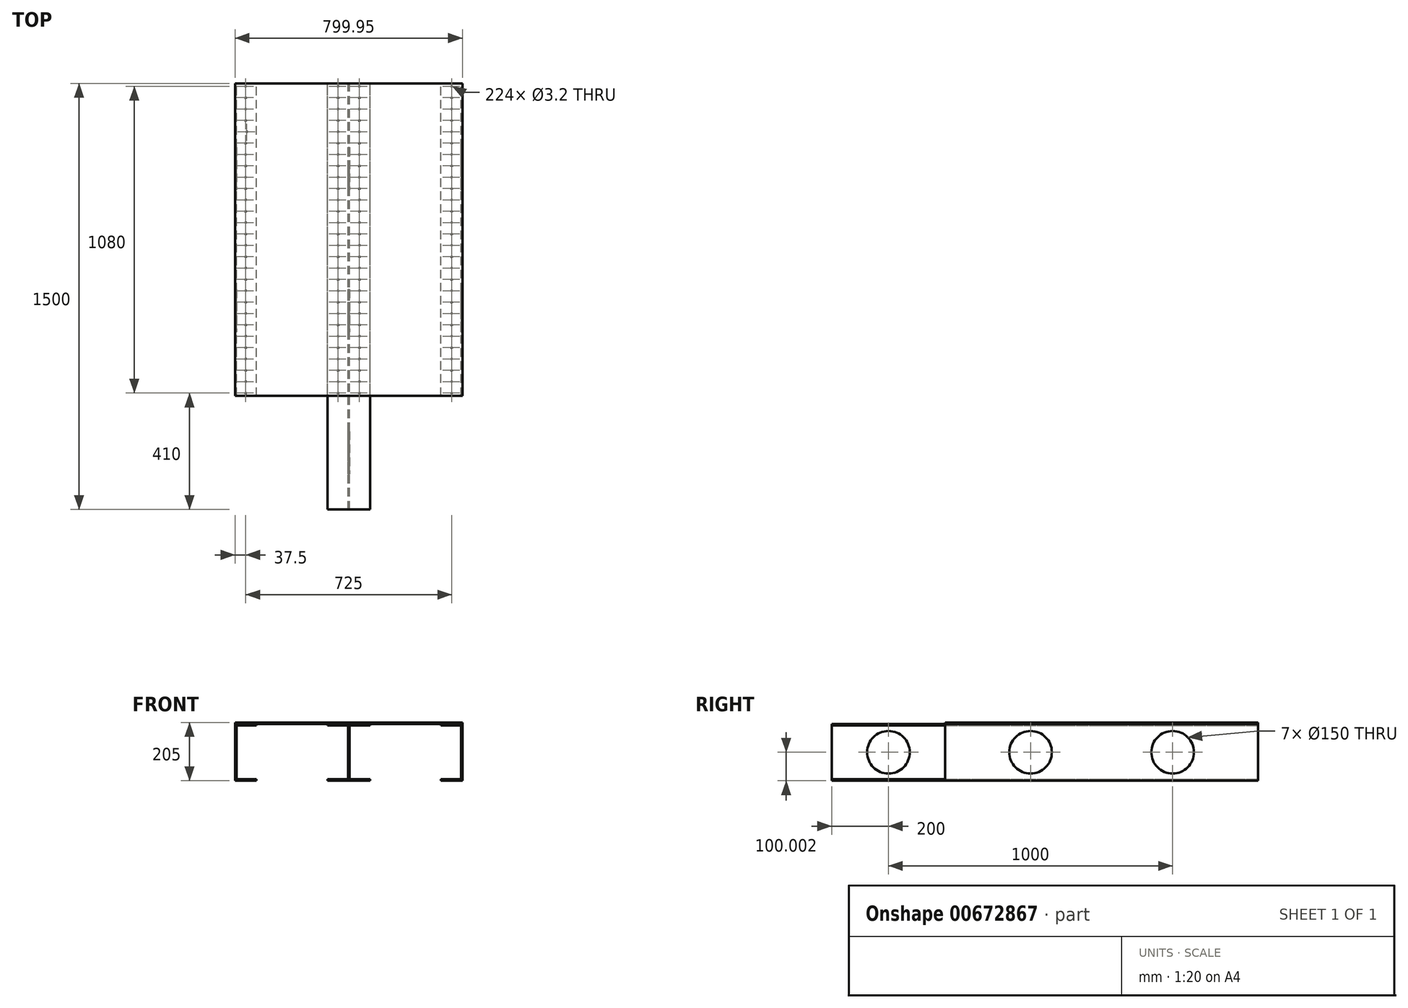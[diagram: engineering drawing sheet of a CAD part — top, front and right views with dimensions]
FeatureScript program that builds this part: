
annotation { "Feature Type Name" : "Feature", "Feature Type Description" : "" }
export const myFeature = defineFeature(function(context is Context, id is Id, definition is map)
    precondition{}
    {
        {
            var Q0;
            Q0=qCreatedBy(makeId("Front.planeOp"),FACE);
            var sketch = newSketch(context, id + "F0", { "sketchPlane" : qUnion([Q0])});
            skLineSegment(sketch, "E0", {"start": v(180.44, 90.06) * mm, "end": v(255.44, 90.06) * mm});
            skLineSegment(sketch, "E1", {"start": v(255.44, -109.94) * mm, "end": v(180.44, -109.94) * mm});
            skLineSegment(sketch, "E2", {"start": v(180.44, -109.94) * mm, "end": v(180.44, -104.94) * mm});
            skLineSegment(sketch, "E3", {"start": v(180.44, -104.94) * mm, "end": v(250.44, -104.94) * mm});
            skLineSegment(sketch, "E4", {"start": v(250.44, -104.94) * mm, "end": v(250.44, 85.06) * mm});
            skLineSegment(sketch, "E5", {"start": v(250.44, 85.06) * mm, "end": v(180.44, 85.06) * mm});
            skLineSegment(sketch, "E6", {"start": v(180.44, 85.06) * mm, "end": v(180.44, 90.06) * mm});
            skLineSegment(sketch, "E7", {"start": v(255.44, 90.06) * mm, "end": v(255.44, -109.94) * mm});
            skSolve(sketch);
        }
        {
            var Q0;
            Q0 = qSketchRegion(id + "F0", true);
            extrude(context, id + "F1", {"entities" : qUnion([Q0]), "depth" : 1100 * mm, "offsetDistance" : 25.4 * mm});
        }
        {
            var Q0;
            Q0=qCreatedBy(makeId("Front.planeOp"),FACE);
            var sketch = newSketch(context, id + "F2", { "sketchPlane" : qUnion([Q0])});
            skLineSegment(sketch, "E8", {"start": v(-469.5, 90.06) * mm, "end": v(-544.5, 90.06) * mm});
            skLineSegment(sketch, "E9", {"start": v(-544.5, 90.06) * mm, "end": v(-544.5, -109.94) * mm});
            skLineSegment(sketch, "E10", {"start": v(-544.5, -109.94) * mm, "end": v(-469.5, -109.94) * mm});
            skLineSegment(sketch, "E11", {"start": v(-469.48, -104.94) * mm, "end": v(-539.5, -104.94) * mm});
            skLineSegment(sketch, "E12", {"start": v(-539.5, -104.94) * mm, "end": v(-539.5, 85.06) * mm});
            skLineSegment(sketch, "E13", {"start": v(-539.5, 85.06) * mm, "end": v(-469.5, 85.06) * mm});
            skLineSegment(sketch, "E14", {"start": v(-469.5, 85.06) * mm, "end": v(-469.5, 90.06) * mm});
            skLineSegment(sketch, "E15", {"start": v(-469.48, -104.94) * mm, "end": v(-469.5, -109.94) * mm});
            skSolve(sketch);
        }
        {
            var Q0;
            Q0 = qSketchRegion(id + "F2", true);
            extrude(context, id + "F3", {"entities" : qUnion([Q0]), "depth" : 1100 * mm, "offsetDistance" : 25.4 * mm});
        }
        {
            var Q0;
            Q0=qCreatedBy(makeId("Front.planeOp"),FACE);
            var sketch = newSketch(context, id + "F4", { "sketchPlane" : qUnion([Q0])});
            skLineSegment(sketch, "E16", {"start": v(-219.5, 90.06) * mm, "end": v(-69.5, 90.06) * mm});
            skLineSegment(sketch, "E17", {"start": v(-69.5, 90.06) * mm, "end": v(-69.5, 85.06) * mm});
            skLineSegment(sketch, "E18", {"start": v(-69.5, 85.06) * mm, "end": v(-142, 85.06) * mm});
            skLineSegment(sketch, "E19", {"start": v(-142, 85.06) * mm, "end": v(-142, -104.94) * mm});
            skLineSegment(sketch, "E20", {"start": v(-142, -104.94) * mm, "end": v(-69.5, -104.94) * mm});
            skLineSegment(sketch, "E21", {"start": v(-69.5, -104.94) * mm, "end": v(-69.5, -109.94) * mm});
            skLineSegment(sketch, "E22", {"start": v(-69.5, -109.94) * mm, "end": v(-219.5, -109.94) * mm});
            skLineSegment(sketch, "E23", {"start": v(-219.5, -109.94) * mm, "end": v(-219.5, -104.94) * mm});
            skLineSegment(sketch, "E24", {"start": v(-219.5, -104.94) * mm, "end": v(-147, -104.94) * mm});
            skLineSegment(sketch, "E25", {"start": v(-147, -104.94) * mm, "end": v(-147, 85.06) * mm});
            skLineSegment(sketch, "E26", {"start": v(-147, 85.06) * mm, "end": v(-219.5, 85.06) * mm});
            skLineSegment(sketch, "E27", {"start": v(-219.5, 85.06) * mm, "end": v(-219.5, 90.06) * mm});
            skSolve(sketch);
        }
        {
            var Q0;
            Q0 = qSketchRegion(id + "F4", true);
            extrude(context, id + "F5", {"entities" : qUnion([Q0]), "depth" : 1500 * mm, "offsetDistance" : 25.4 * mm});
        }
        {
            var Q0;
            Q0=qCreatedBy(makeId("Front.planeOp"),FACE);
            var sketch = newSketch(context, id + "F6", { "sketchPlane" : qUnion([Q0])});
            skLineSegment(sketch, "E28.bottom", {"start": v(-544.5, 90.06) * mm, "end": v(255.44, 90.06) * mm});
            skLineSegment(sketch, "E28.top", {"start": v(-544.5, 95.06) * mm, "end": v(255.44, 95.06) * mm});
            skLineSegment(sketch, "E28.left", {"start": v(-544.5, 90.06) * mm, "end": v(-544.5, 95.06) * mm});
            skLineSegment(sketch, "E28.right", {"start": v(255.44, 90.06) * mm, "end": v(255.44, 95.06) * mm});
            skSolve(sketch);
        }
        {
            var Q0;
            Q0 = qSketchRegion(id + "F6", true);
            extrude(context, id + "F7", {"entities" : qUnion([Q0]), "depth" : 1100 * mm, "offsetDistance" : 25.4 * mm});
        }
        {
            var Q0;
            Q0=makeQuery(id+"F1.opExtrude","SWEPT_FACE",FACE,{"disambiguationData":[OSD([sQuery(id+"F0.wireOp",EDGE,"E7")])]});
            var sketch = newSketch(context, id + "F8", { "sketchPlane" : qUnion([Q0])});
            skCircle(sketch, "E29", {"center": v(-300, -9.94) * mm, "radius": 75 * mm});
            skSolve(sketch);
        }
        {
            var Q0;
            Q0=makeQuery(id+"F8.imprint","IMPRINT",FACE,{"disambiguationData":[TD([[makeQuery(id+"F8.imprint","IMPRINT",EDGE,{"derivedFrom":sQuery(id+"F8.wireOp",EDGE,"E29")}),1.0]])]});
            extrude(context, id + "F9", {"entities" : qUnion([Q0]), "operationType" : NewBodyOperationType.REMOVE, "oppositeDirection" : true, "depth" : 5 * mm, "offsetDistance" : 25.4 * mm});
        }
        {
            var Q0;
            Q0=makeQuery(id+"F1.opExtrude","SWEPT_FACE",FACE,{"disambiguationData":[OSD([sQuery(id+"F0.wireOp",EDGE,"E7")])]});
            var sketch = newSketch(context, id + "F10", { "sketchPlane" : qUnion([Q0])});
            skCircle(sketch, "E30", {"center": v(-800, -9.94) * mm, "radius": 75 * mm});
            skSolve(sketch);
        }
        {
            var Q0;
            Q0 = qSketchRegion(id + "F10", true);
            extrude(context, id + "F11", {"entities" : qUnion([Q0]), "operationType" : NewBodyOperationType.REMOVE, "oppositeDirection" : true, "depth" : 5 * mm, "offsetDistance" : 25.4 * mm});
        }
        {
            var Q0;
            Q0=makeQuery(id+"F3.opExtrude","SWEPT_FACE",FACE,{"disambiguationData":[OSD([sQuery(id+"F2.wireOp",EDGE,"E9")])]});
            var sketch = newSketch(context, id + "F12", { "sketchPlane" : qUnion([Q0])});
            skCircle(sketch, "E31", {"center": v(300, -9.94) * mm, "radius": 75 * mm});
            skCircle(sketch, "E32", {"center": v(800, -9.94) * mm, "radius": 75 * mm});
            skSolve(sketch);
        }
        {
            var Q0;
            Q0=makeQuery(id+"F12.imprint","IMPRINT",FACE,{"disambiguationData":[TD([[makeQuery(id+"F12.imprint","IMPRINT",EDGE,{"derivedFrom":sQuery(id+"F12.wireOp",EDGE,"E31")}),1.0]])]});
            var Q1;
            Q1=makeQuery(id+"F12.imprint","IMPRINT",FACE,{"disambiguationData":[TD([[makeQuery(id+"F12.imprint","IMPRINT",EDGE,{"derivedFrom":sQuery(id+"F12.wireOp",EDGE,"E32")}),1.0]])]});
            extrude(context, id + "F13", {"entities" : qUnion([Q0, Q1]), "operationType" : NewBodyOperationType.REMOVE, "oppositeDirection" : true, "depth" : 5 * mm, "offsetDistance" : 25.4 * mm});
        }
        {
            var Q0;
            Q0=makeQuery(id+"F5.opExtrude","SWEPT_FACE",FACE,{"disambiguationData":[OSD([sQuery(id+"F4.wireOp",EDGE,"E19")])]});
            var sketch = newSketch(context, id + "F14", { "sketchPlane" : qUnion([Q0])});
            skCircle(sketch, "E33", {"center": v(-800, -9.94) * mm, "radius": 75 * mm});
            skCircle(sketch, "E34", {"center": v(-300, -9.94) * mm, "radius": 75 * mm});
            skCircle(sketch, "E35", {"center": v(-1300, -9.94) * mm, "radius": 75 * mm});
            skSolve(sketch);
        }
        {
            var Q0;
            Q0=makeQuery(id+"F14.imprint","IMPRINT",FACE,{"disambiguationData":[TD([[makeQuery(id+"F14.imprint","IMPRINT",EDGE,{"derivedFrom":sQuery(id+"F14.wireOp",EDGE,"E35")}),1.0]])]});
            var Q1;
            Q1=makeQuery(id+"F14.imprint","IMPRINT",FACE,{"disambiguationData":[TD([[makeQuery(id+"F14.imprint","IMPRINT",EDGE,{"derivedFrom":sQuery(id+"F14.wireOp",EDGE,"E33")}),1.0]])]});
            var Q2;
            Q2=makeQuery(id+"F14.imprint","IMPRINT",FACE,{"disambiguationData":[TD([[makeQuery(id+"F14.imprint","IMPRINT",EDGE,{"derivedFrom":sQuery(id+"F14.wireOp",EDGE,"E34")}),1.0]])]});
            extrude(context, id + "F15", {"entities" : qUnion([Q0, Q1, Q2]), "operationType" : NewBodyOperationType.REMOVE, "oppositeDirection" : true, "depth" : 5 * mm, "offsetDistance" : 25.4 * mm});
        }
        {
            var Q0;
            Q0=makeQuery(id+"F7.opExtrude","SWEPT_FACE",FACE,{"disambiguationData":[OSD([sQuery(id+"F6.wireOp",EDGE,"E28.top")])]});
            var sketch = newSketch(context, id + "F16", { "sketchPlane" : qUnion([Q0])});
            skCircle(sketch, "E36", {"center": v(-507, -1090) * mm, "radius": 1.6 * mm});
            skCircle(sketch, "E37", {"center": v(-507, -1050) * mm, "radius": 1.6 * mm});
            skCircle(sketch, "E38", {"center": v(-507, -1010) * mm, "radius": 1.6 * mm});
            skCircle(sketch, "E39", {"center": v(-507, -970) * mm, "radius": 1.6 * mm});
            skCircle(sketch, "E40", {"center": v(-507, -930) * mm, "radius": 1.6 * mm});
            skCircle(sketch, "E41", {"center": v(-507, -890) * mm, "radius": 1.6 * mm});
            skCircle(sketch, "E42", {"center": v(-507, -850) * mm, "radius": 1.6 * mm});
            skCircle(sketch, "E43", {"center": v(-507, -810) * mm, "radius": 1.6 * mm});
            skCircle(sketch, "E44", {"center": v(-507, -770) * mm, "radius": 1.6 * mm});
            skCircle(sketch, "E45", {"center": v(-507, -730) * mm, "radius": 1.6 * mm});
            skCircle(sketch, "E46", {"center": v(-507, -690) * mm, "radius": 1.6 * mm});
            skCircle(sketch, "E47", {"center": v(-507, -650) * mm, "radius": 1.6 * mm});
            skCircle(sketch, "E48", {"center": v(-507, -610) * mm, "radius": 1.6 * mm});
            skCircle(sketch, "E49", {"center": v(-507, -570) * mm, "radius": 1.6 * mm});
            skCircle(sketch, "E50", {"center": v(-507, -530) * mm, "radius": 1.6 * mm});
            skCircle(sketch, "E51", {"center": v(-507, -490) * mm, "radius": 1.6 * mm});
            skCircle(sketch, "E52", {"center": v(-507, -450) * mm, "radius": 1.6 * mm});
            skCircle(sketch, "E53", {"center": v(-507, -410) * mm, "radius": 1.6 * mm});
            skCircle(sketch, "E54", {"center": v(-507, -290) * mm, "radius": 1.6 * mm});
            skCircle(sketch, "E55", {"center": v(-507, -330) * mm, "radius": 1.6 * mm});
            skCircle(sketch, "E56", {"center": v(-507, -370) * mm, "radius": 1.6 * mm});
            skCircle(sketch, "E57", {"center": v(-507, -250) * mm, "radius": 1.6 * mm});
            skCircle(sketch, "E58", {"center": v(-507, -210) * mm, "radius": 1.6 * mm});
            skCircle(sketch, "E59", {"center": v(-507, -130) * mm, "radius": 1.6 * mm});
            skCircle(sketch, "E60", {"center": v(-503.1, -170) * mm, "radius": 1.6 * mm});
            skCircle(sketch, "E61", {"center": v(-507, -90) * mm, "radius": 1.6 * mm});
            skCircle(sketch, "E62", {"center": v(-507, -50) * mm, "radius": 1.6 * mm});
            skCircle(sketch, "E63", {"center": v(-507, -10) * mm, "radius": 1.6 * mm});
            skCircle(sketch, "E64", {"center": v(-182, -1090) * mm, "radius": 1.6 * mm});
            skCircle(sketch, "E65", {"center": v(-182, -1050) * mm, "radius": 1.6 * mm});
            skCircle(sketch, "E66", {"center": v(-182, -1010) * mm, "radius": 1.6 * mm});
            skCircle(sketch, "E67", {"center": v(-182, -970) * mm, "radius": 1.6 * mm});
            skCircle(sketch, "E68", {"center": v(-182, -930) * mm, "radius": 1.6 * mm});
            skCircle(sketch, "E69", {"center": v(-182, -890) * mm, "radius": 1.6 * mm});
            skCircle(sketch, "E70", {"center": v(-182, -850) * mm, "radius": 1.6 * mm});
            skCircle(sketch, "E71", {"center": v(-182, -810) * mm, "radius": 1.6 * mm});
            skCircle(sketch, "E72", {"center": v(-182, -770) * mm, "radius": 1.6 * mm});
            skCircle(sketch, "E73", {"center": v(-182, -730) * mm, "radius": 1.6 * mm});
            skCircle(sketch, "E74", {"center": v(-182, -690) * mm, "radius": 1.6 * mm});
            skCircle(sketch, "E75", {"center": v(-182, -650) * mm, "radius": 1.6 * mm});
            skCircle(sketch, "E76", {"center": v(-182, -610) * mm, "radius": 1.6 * mm});
            skCircle(sketch, "E77", {"center": v(-182, -570) * mm, "radius": 1.6 * mm});
            skCircle(sketch, "E78", {"center": v(-182, -530) * mm, "radius": 1.6 * mm});
            skCircle(sketch, "E79", {"center": v(-182, -490) * mm, "radius": 1.6 * mm});
            skCircle(sketch, "E80", {"center": v(-182, -450) * mm, "radius": 1.6 * mm});
            skCircle(sketch, "E81", {"center": v(-182, -410) * mm, "radius": 1.6 * mm});
            skCircle(sketch, "E82", {"center": v(-182, -290) * mm, "radius": 1.6 * mm});
            skCircle(sketch, "E83", {"center": v(-182, -330) * mm, "radius": 1.6 * mm});
            skCircle(sketch, "E84", {"center": v(-182, -370) * mm, "radius": 1.6 * mm});
            skCircle(sketch, "E85", {"center": v(-182, -250) * mm, "radius": 1.6 * mm});
            skCircle(sketch, "E86", {"center": v(-182, -210) * mm, "radius": 1.6 * mm});
            skCircle(sketch, "E87", {"center": v(-182, -130) * mm, "radius": 1.6 * mm});
            skCircle(sketch, "E88", {"center": v(-182, -170) * mm, "radius": 1.6 * mm});
            skCircle(sketch, "E89", {"center": v(-182, -90) * mm, "radius": 1.6 * mm});
            skCircle(sketch, "E90", {"center": v(-182, -50) * mm, "radius": 1.6 * mm});
            skCircle(sketch, "E91", {"center": v(-182, -10) * mm, "radius": 1.6 * mm});
            skCircle(sketch, "E92", {"center": v(-107, -1090) * mm, "radius": 1.6 * mm});
            skCircle(sketch, "E93", {"center": v(-107, -1050) * mm, "radius": 1.6 * mm});
            skCircle(sketch, "E94", {"center": v(-107, -1010) * mm, "radius": 1.6 * mm});
            skCircle(sketch, "E95", {"center": v(-107, -970) * mm, "radius": 1.6 * mm});
            skCircle(sketch, "E96", {"center": v(-107, -930) * mm, "radius": 1.6 * mm});
            skCircle(sketch, "E97", {"center": v(-107, -890) * mm, "radius": 1.6 * mm});
            skCircle(sketch, "E98", {"center": v(-107, -850) * mm, "radius": 1.6 * mm});
            skCircle(sketch, "E99", {"center": v(-107, -810) * mm, "radius": 1.6 * mm});
            skCircle(sketch, "E100", {"center": v(-107, -770) * mm, "radius": 1.6 * mm});
            skCircle(sketch, "E101", {"center": v(-107, -730) * mm, "radius": 1.6 * mm});
            skCircle(sketch, "E102", {"center": v(-107, -690) * mm, "radius": 1.6 * mm});
            skCircle(sketch, "E103", {"center": v(-107, -650) * mm, "radius": 1.6 * mm});
            skCircle(sketch, "E104", {"center": v(-107, -610) * mm, "radius": 1.6 * mm});
            skCircle(sketch, "E105", {"center": v(-107, -570) * mm, "radius": 1.6 * mm});
            skCircle(sketch, "E106", {"center": v(-107, -530) * mm, "radius": 1.6 * mm});
            skCircle(sketch, "E107", {"center": v(-107, -490) * mm, "radius": 1.6 * mm});
            skCircle(sketch, "E108", {"center": v(-107, -450) * mm, "radius": 1.6 * mm});
            skCircle(sketch, "E109", {"center": v(-107, -410) * mm, "radius": 1.6 * mm});
            skCircle(sketch, "E110", {"center": v(-107, -290) * mm, "radius": 1.6 * mm});
            skCircle(sketch, "E111", {"center": v(-107, -330) * mm, "radius": 1.6 * mm});
            skCircle(sketch, "E112", {"center": v(-107, -370) * mm, "radius": 1.6 * mm});
            skCircle(sketch, "E113", {"center": v(-107, -250) * mm, "radius": 1.6 * mm});
            skCircle(sketch, "E114", {"center": v(-107, -210) * mm, "radius": 1.6 * mm});
            skCircle(sketch, "E115", {"center": v(-107, -130) * mm, "radius": 1.6 * mm});
            skCircle(sketch, "E116", {"center": v(-107, -170) * mm, "radius": 1.6 * mm});
            skCircle(sketch, "E117", {"center": v(-107, -90) * mm, "radius": 1.6 * mm});
            skCircle(sketch, "E118", {"center": v(-107, -50) * mm, "radius": 1.6 * mm});
            skCircle(sketch, "E119", {"center": v(-107, -10) * mm, "radius": 1.6 * mm});
            skCircle(sketch, "E120", {"center": v(218, -1090) * mm, "radius": 1.6 * mm});
            skCircle(sketch, "E121", {"center": v(218, -1050) * mm, "radius": 1.6 * mm});
            skCircle(sketch, "E122", {"center": v(218, -1010) * mm, "radius": 1.6 * mm});
            skCircle(sketch, "E123", {"center": v(218, -970) * mm, "radius": 1.6 * mm});
            skCircle(sketch, "E124", {"center": v(218, -930) * mm, "radius": 1.6 * mm});
            skCircle(sketch, "E125", {"center": v(218, -890) * mm, "radius": 1.6 * mm});
            skCircle(sketch, "E126", {"center": v(218, -850) * mm, "radius": 1.6 * mm});
            skCircle(sketch, "E127", {"center": v(218, -810) * mm, "radius": 1.6 * mm});
            skCircle(sketch, "E128", {"center": v(218, -770) * mm, "radius": 1.6 * mm});
            skCircle(sketch, "E129", {"center": v(218, -730) * mm, "radius": 1.6 * mm});
            skCircle(sketch, "E130", {"center": v(218, -690) * mm, "radius": 1.6 * mm});
            skCircle(sketch, "E131", {"center": v(218, -650) * mm, "radius": 1.6 * mm});
            skCircle(sketch, "E132", {"center": v(218, -610) * mm, "radius": 1.6 * mm});
            skCircle(sketch, "E133", {"center": v(218, -570) * mm, "radius": 1.6 * mm});
            skCircle(sketch, "E134", {"center": v(218, -530) * mm, "radius": 1.6 * mm});
            skCircle(sketch, "E135", {"center": v(218, -490) * mm, "radius": 1.6 * mm});
            skCircle(sketch, "E136", {"center": v(218, -450) * mm, "radius": 1.6 * mm});
            skCircle(sketch, "E137", {"center": v(218, -410) * mm, "radius": 1.6 * mm});
            skCircle(sketch, "E138", {"center": v(218, -290) * mm, "radius": 1.6 * mm});
            skCircle(sketch, "E139", {"center": v(218, -330) * mm, "radius": 1.6 * mm});
            skCircle(sketch, "E140", {"center": v(218, -370) * mm, "radius": 1.6 * mm});
            skCircle(sketch, "E141", {"center": v(218, -250) * mm, "radius": 1.6 * mm});
            skCircle(sketch, "E142", {"center": v(218, -210) * mm, "radius": 1.6 * mm});
            skCircle(sketch, "E143", {"center": v(218, -130) * mm, "radius": 1.6 * mm});
            skCircle(sketch, "E144", {"center": v(218, -170) * mm, "radius": 1.6 * mm});
            skCircle(sketch, "E145", {"center": v(218, -90) * mm, "radius": 1.6 * mm});
            skCircle(sketch, "E146", {"center": v(218, -50) * mm, "radius": 1.6 * mm});
            skCircle(sketch, "E147", {"center": v(218, -10) * mm, "radius": 1.6 * mm});
            skSolve(sketch);
        }
        {
            var Q0;
            Q0 = qSketchRegion(id + "F16", true);
            extrude(context, id + "F17", {"entities" : qUnion([Q0]), "operationType" : NewBodyOperationType.REMOVE, "oppositeDirection" : true, "depth" : 50 * mm, "offsetDistance" : 25.4 * mm});
        }
    });
